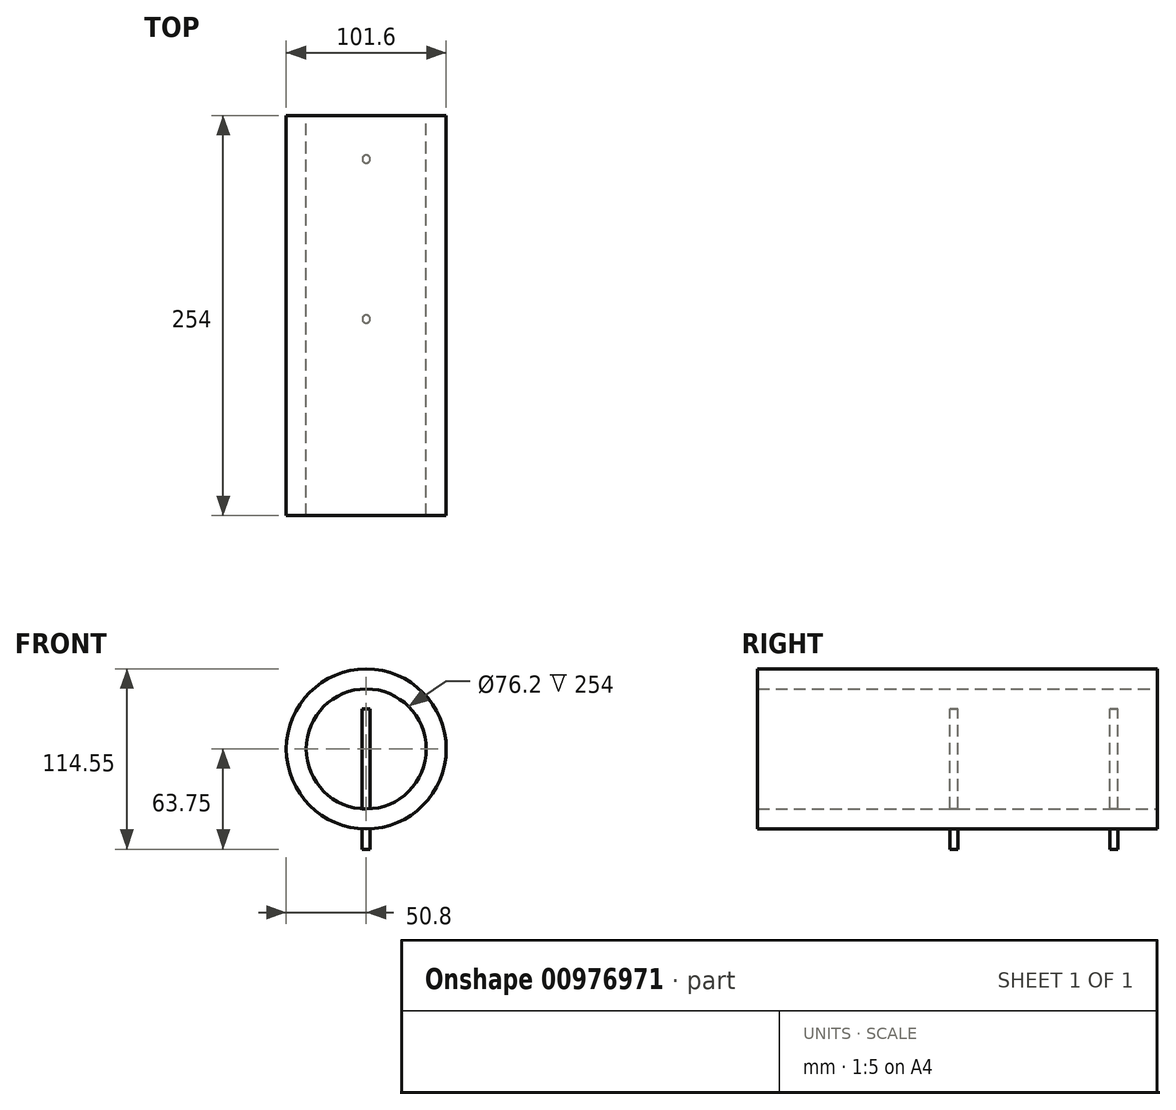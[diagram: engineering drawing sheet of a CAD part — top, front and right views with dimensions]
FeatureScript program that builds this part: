
annotation { "Feature Type Name" : "Feature", "Feature Type Description" : "" }
export const myFeature = defineFeature(function(context is Context, id is Id, definition is map)
    precondition{}
    {
        {
            var Q0;
            Q0=qCreatedBy(makeId("Front.planeOp"),FACE);
            var sketch = newSketch(context, id + "F0", { "sketchPlane" : qUnion([Q0])});
            skCircle(sketch, "E0", {"center": v(0, 0) * mm, "radius": 50.8 * mm});
            skCircle(sketch, "E1", {"center": v(0, 0) * mm, "radius": 38.1 * mm});
            skSolve(sketch);
        }
        {
            var Q0;
            Q0 = qSketchRegion(id + "F0", true);
            extrude(context, id + "F1", {"entities" : qUnion([Q0]), "depth" : 254 * mm, "offsetDistance" : 25.4 * mm});
        }
        {
            var Q0;
            Q0=qCreatedBy(makeId("Top.planeOp"),FACE);
            var sketch = newSketch(context, id + "F2", { "sketchPlane" : qUnion([Q0])});
            skCircle(sketch, "E2", {"center": v(0, -27.64) * mm, "radius": 2.5 * mm});
            skCircle(sketch, "E3", {"center": v(0, -129.24) * mm, "radius": 2.5 * mm});
            skSolve(sketch);
        }
        {
            var Q0;
            Q0 = qSketchRegion(id + "F2", true);
            extrude(context, id + "F3", {"entities" : qUnion([Q0]), "operationType" : NewBodyOperationType.ADD, "oppositeDirection" : true, "depth" : 63.75 * mm, "offsetDistance" : 25.4 * mm, "hasSecondDirection" : true, "secondDirectionOppositeDirection" : false, "secondDirectionDepth" : 25.4 * mm});
        }
    });
